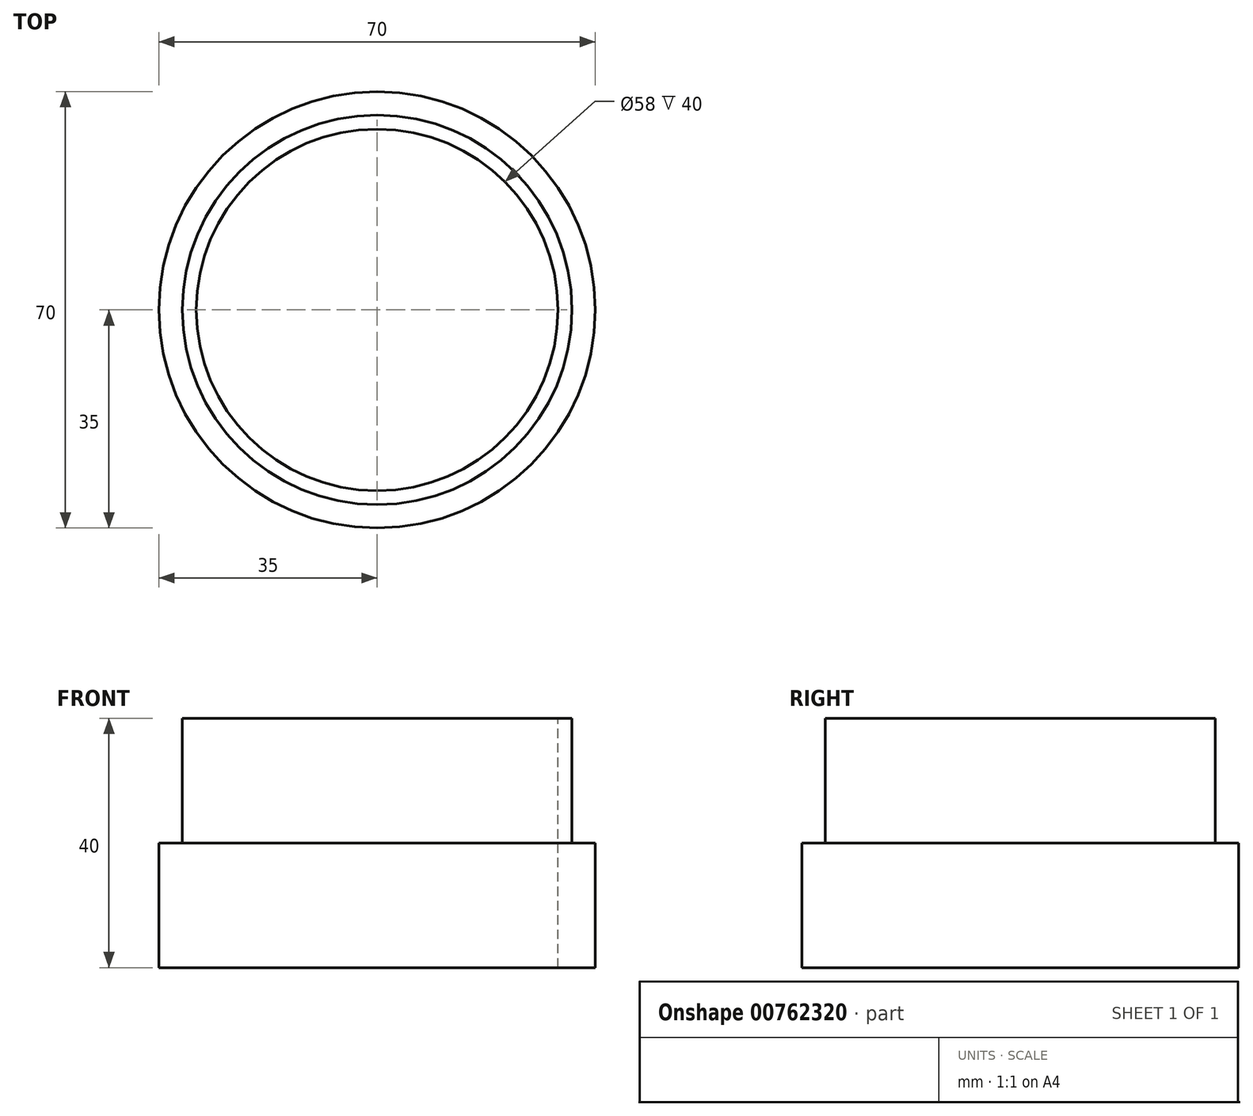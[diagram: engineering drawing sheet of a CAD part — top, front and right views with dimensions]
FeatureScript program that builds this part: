
annotation { "Feature Type Name" : "Feature", "Feature Type Description" : "" }
export const myFeature = defineFeature(function(context is Context, id is Id, definition is map)
    precondition{}
    {
        {
            var Q0;
            Q0=qCreatedBy(makeId("Top.planeOp"),FACE);
            var sketch = newSketch(context, id + "F0", { "sketchPlane" : qUnion([Q0])});
            skCircle(sketch, "E0", {"center": v(0, 0) * mm, "radius": 35 * mm});
            skSolve(sketch);
        }
        {
            var Q0;
            Q0=makeQuery(id+"F0.imprint","IMPRINT",FACE,{"disambiguationData":[TD([[makeQuery(id+"F0.imprint","IMPRINT",EDGE,{"derivedFrom":sQuery(id+"F0.wireOp",EDGE,"E0")}),1.0]])]});
            extrude(context, id + "F1", {"entities" : qUnion([Q0]), "depth" : 40 * mm, "offsetDistance" : 25 * mm});
        }
        {
            var Q0;
            Q0=makeQuery(id+"F1.opExtrude","CAP_FACE",FACE,{"disambiguationData":[OSD([sQuery(id+"F0.wireOp",EDGE,"E0")])],"isStart":false});
            var sketch = newSketch(context, id + "F2", { "sketchPlane" : qUnion([Q0])});
            skCircle(sketch, "E1", {"center": v(0, 0) * mm, "radius": 31.25 * mm});
            skCircle(sketch, "E2", {"center": v(0, 0) * mm, "radius": 29 * mm});
            skCircle(sketch, "E3", {"center": v(0, 0) * mm, "radius": 35 * mm});
            skSolve(sketch);
        }
        {
            var Q0;
            Q0=makeQuery(id+"F2.imprint","IMPRINT",FACE,{"disambiguationData":[TD([[makeQuery(id+"F2.imprint","IMPRINT",EDGE,{"derivedFrom":sQuery(id+"F2.wireOp",EDGE,"E1")}),-1.0]])]});
            extrude(context, id + "F3", {"entities" : qUnion([Q0]), "operationType" : NewBodyOperationType.REMOVE, "oppositeDirection" : true, "depth" : 20 * mm, "offsetDistance" : 25 * mm});
        }
        {
            var Q0;
            Q0=makeQuery(id+"F2.imprint","IMPRINT",FACE,{"disambiguationData":[TD([[makeQuery(id+"F2.imprint","IMPRINT",EDGE,{"derivedFrom":sQuery(id+"F2.wireOp",EDGE,"E2")}),1.0]])]});
            extrude(context, id + "F4", {"entities" : qUnion([Q0]), "operationType" : NewBodyOperationType.REMOVE, "oppositeDirection" : true, "depth" : 40 * mm, "offsetDistance" : 25 * mm});
        }
    });
